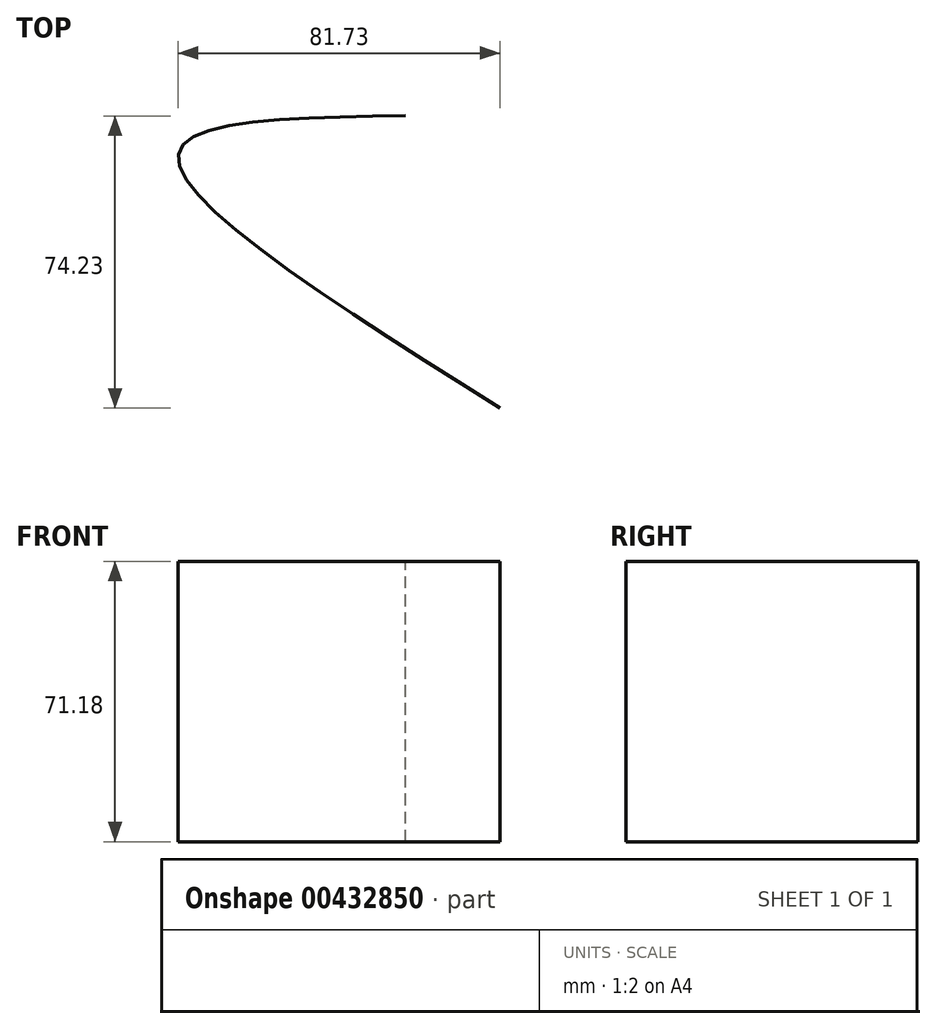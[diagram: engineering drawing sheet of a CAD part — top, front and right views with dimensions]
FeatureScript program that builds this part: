
annotation { "Feature Type Name" : "Feature", "Feature Type Description" : "" }
export const myFeature = defineFeature(function(context is Context, id is Id, definition is map)
    precondition{}
    {
        {
            var Q0;
            Q0=qCreatedBy(makeId("Top.planeOp"),FACE);
            var sketch = newSketch(context, id + "F0", { "sketchPlane" : qUnion([Q0])});
            skFitSpline(sketch, "E0", {"points": [v(37.32, -27) * mm, v(-44.26, 37.83) * mm, v(13.37, 47.23) * mm], "startDerivative": vector(-221.92, 139.49) * mm, "endDerivative": vector(193.95, 2.4) * mm});
            skSolve(sketch);
        }
        {
            var Q0;
            Q0=qCreatedBy(makeId("Right.planeOp"),FACE);
            var sketch = newSketch(context, id + "F1", { "sketchPlane" : qUnion([Q0])});
            skSolve(sketch);
        }
        {
            var Q0;
            Q0 = qSketchRegion(id + "F1", true);
            var Q1;
            Q1=sQuery(id+"F0.wireOp",EDGE,"E0");
            extrude(context, id + "F2", {"entities" : qUnion([Q0]), "bodyType" : ToolBodyType.SURFACE, "surfaceEntities" : qUnion([Q1]), "depth" : 71.18 * mm, "offsetDistance" : 25.4 * mm});
        }
    });
